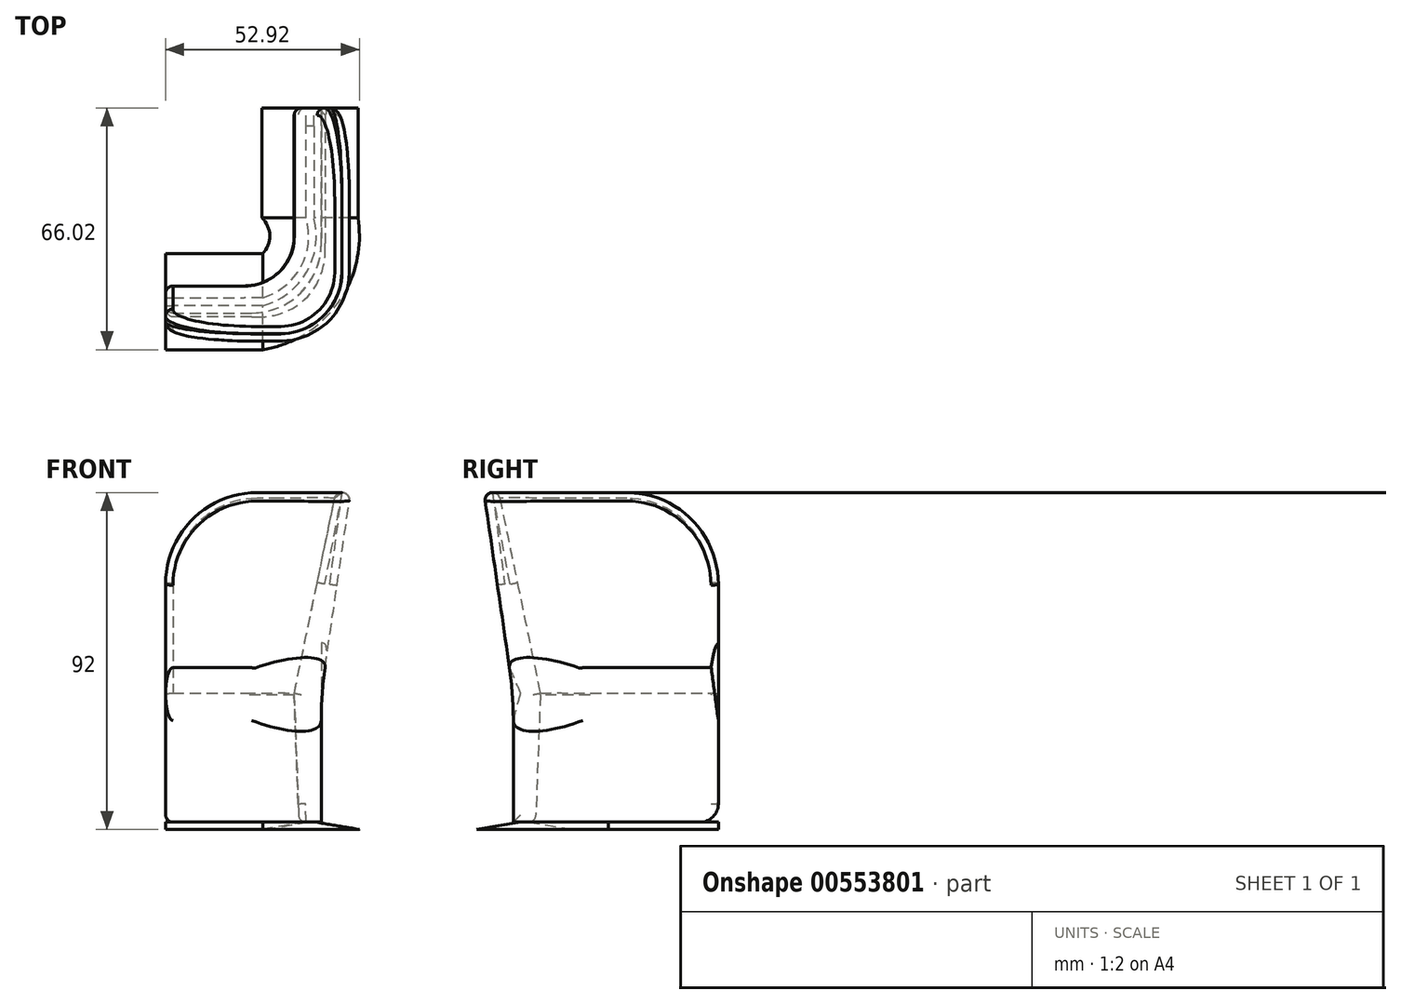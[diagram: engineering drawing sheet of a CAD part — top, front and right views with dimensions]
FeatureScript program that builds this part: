
annotation { "Feature Type Name" : "Feature", "Feature Type Description" : "" }
export const myFeature = defineFeature(function(context is Context, id is Id, definition is map)
    precondition{}
    {
        {
            var Q0;
            Q0=qCreatedBy(makeId("Top.planeOp"),FACE);
            var sketch = newSketch(context, id + "F0", { "sketchPlane" : qUnion([Q0])});
            skLineSegment(sketch, "E0", {"start": v(0, -50) * mm, "end": v(0, -15) * mm});
            skLineSegment(sketch, "E1", {"start": v(-15, 0) * mm, "end": v(-40, 0) * mm});
            skLineSegment(sketch, "E2", {"start": v(-40, 0) * mm, "end": v(-40, 6) * mm});
            skLineSegment(sketch, "E3", {"start": v(-40, 6) * mm, "end": v(-13, 6) * mm});
            skLineSegment(sketch, "E4", {"start": v(6, -13) * mm, "end": v(6, -50) * mm});
            skLineSegment(sketch, "E5", {"start": v(6, -50) * mm, "end": v(0, -50) * mm});
            skPoint(sketch, "E6.visualSharp", {"position": v(0, 0) * mm});
            skArc(sketch, "E6.filletArc", {"start": v(0, -15) * mm, "mid": v(-4.4, -4.4) * mm, "end": v(-15, 0) * mm});
            skArc(sketch, "E7.filletArc", {"start": v(6, -13) * mm, "mid": v(0.44, 0.44) * mm, "end": v(-13, 6) * mm});
            skSolve(sketch);
        }
        {
            var Q0;
            Q0=makeQuery(id+"F0.imprint","IMPRINT",FACE,{"disambiguationData":[TD([[makeQuery(id+"F0.imprint","IMPRINT",EDGE,{"derivedFrom":sQuery(id+"F0.wireOp",EDGE,"E0")}),-1.0]])]});
            extrude(context, id + "F1", {"entities" : qUnion([Q0]), "depth" : 40 * mm});
        }
        {
            var Q0;
            Q0=makeQuery(id+"F1.opExtrude","CAP_FACE",FACE,{"disambiguationData":[OSD([sQuery(id+"F0.wireOp",EDGE,"E0"),sQuery(id+"F0.wireOp",EDGE,"E1"),sQuery(id+"F0.wireOp",EDGE,"E2"),sQuery(id+"F0.wireOp",EDGE,"E3"),sQuery(id+"F0.wireOp",EDGE,"E4"),sQuery(id+"F0.wireOp",EDGE,"E5"),sQuery(id+"F0.wireOp",EDGE,"E6.filletArc"),sQuery(id+"F0.wireOp",EDGE,"E7.filletArc")])],"isStart":false});
            var sketch = newSketch(context, id + "F2", { "sketchPlane" : qUnion([Q0])});
            skLineSegment(sketch, "E8.0", {"start": v(-15, -1.5) * mm, "end": v(-40, -1.5) * mm});
            skArc(sketch, "E8.1", {"start": v(-1.5, -15) * mm, "mid": v(-5.45, -5.45) * mm, "end": v(-15, -1.5) * mm});
            skLineSegment(sketch, "E8.2", {"start": v(-1.5, -50) * mm, "end": v(-1.5, -15) * mm});
            skLineSegment(sketch, "E9", {"start": v(-40, -1.5) * mm, "end": v(-40, 6) * mm});
            skLineSegment(sketch, "E10", {"start": v(-1.5, -50) * mm, "end": v(6, -50) * mm});
            skLineSegment(sketch, "E11.0", {"start": v(-40, 6) * mm, "end": v(-13, 6) * mm});
            skArc(sketch, "E11.1", {"start": v(6, -13) * mm, "mid": v(0.44, 0.44) * mm, "end": v(-13, 6) * mm});
            skLineSegment(sketch, "E11.2", {"start": v(6, -13) * mm, "end": v(6, -50) * mm});
            skSolve(sketch);
        }
        {
            var Q0;
            Q0=makeQuery(id+"F1.opExtrude","SWEPT_FACE",FACE,{"disambiguationData":[OSD([sQuery(id+"F0.wireOp",EDGE,"E2")])]});
            var sketch = newSketch(context, id + "F3", { "sketchPlane" : qUnion([Q0])});
            skLineSegment(sketch, "E12", {"start": v(1.5, 40) * mm, "end": v(0, 0) * mm});
            skLineSegment(sketch, "E13", {"start": v(1.5, 40) * mm, "end": v(0, 40) * mm});
            skLineSegment(sketch, "E14", {"start": v(0, 40) * mm, "end": v(0, 0) * mm});
            skSolve(sketch);
        }
        {
            var Q0;
            Q0=makeQuery(id+"F1.opExtrude","SWEPT_FACE",FACE,{"disambiguationData":[OSD([sQuery(id+"F0.wireOp",EDGE,"E5")])]});
            var sketch = newSketch(context, id + "F4", { "sketchPlane" : qUnion([Q0])});
            skLineSegment(sketch, "E15", {"start": v(0, 0) * mm, "end": v(-1.5, 40) * mm});
            skLineSegment(sketch, "E16", {"start": v(-1.5, 40) * mm, "end": v(0, 40) * mm});
            skLineSegment(sketch, "E17", {"start": v(0, 40) * mm, "end": v(0, 0) * mm});
            skSolve(sketch);
        }
        {
            var Q0;
            Q0=makeQuery(id+"F3.imprint","IMPRINT",FACE,{"disambiguationData":[TD([[makeQuery(id+"F3.imprint","IMPRINT",EDGE,{"derivedFrom":sQuery(id+"F3.wireOp",EDGE,"E12")}),-1.0]])]});
            extrude(context, id + "F5", {"entities" : qUnion([Q0]), "oppositeDirection" : true, "depth" : 25 * mm});
        }
        {
            var Q0;
            Q0=sQuery(id+"F0.wireOp",VERTEX,"E6.filletArc.center");
            var Q1;
            Q1=makeQuery(id+"F5.opExtrude","CAP_EDGE",EDGE,{"disambiguationData":[OSD([sQuery(id+"F3.wireOp",EDGE,"E12")])],"isStart":false});
            cPlane(context, id + "F6", {"entities" : qUnion([Q0, Q1]), "cplaneType" : CPlaneType.LINE_ANGLE, "offset" : 25 * mm, "angle" : 0 * degree, "width" : 150 * mm, "height" : 150 * mm});
        }
        {
            var Q0;
            Q0=qCreatedBy(id+"F6.planeOp",FACE);
            var sketch = newSketch(context, id + "F7", { "sketchPlane" : qUnion([Q0])});
            skLineSegment(sketch, "E18", {"start": v(15, 0) * mm, "end": v(15, 39.86) * mm, "construction": true});
            skSolve(sketch);
        }
        {
            var Q0;
            Q0=makeQuery(id+"F5.opExtrude","CAP_FACE",FACE,{"disambiguationData":[OSD([sQuery(id+"F3.wireOp",EDGE,"E12"),sQuery(id+"F3.wireOp",EDGE,"E13"),sQuery(id+"F3.wireOp",EDGE,"E14")])],"isStart":false});
            var sketch = newSketch(context, id + "F8", { "sketchPlane" : qUnion([Q0])});
            skLineSegment(sketch, "E19.0", {"start": v(-1.5, 40) * mm, "end": v(0, 0) * mm});
            skLineSegment(sketch, "E19.1", {"start": v(-1.5, 40) * mm, "end": v(0, 40) * mm});
            skLineSegment(sketch, "E19.2", {"start": v(0, 40) * mm, "end": v(0, 0) * mm});
            skSolve(sketch);
        }
        {
            var Q0;
            Q0=makeQuery(id+"F8.imprint","IMPRINT",FACE,{"disambiguationData":[TD([[makeQuery(id+"F8.imprint","IMPRINT",EDGE,{"derivedFrom":sQuery(id+"F8.wireOp",EDGE,"E19.0")}),1.0]])]});
            var Q1;
            Q1=sQuery(id+"F7.wireOp",EDGE,"E18");
            revolve(context, id + "F9", {"entities" : qUnion([Q0]), "axis" : qUnion([Q1]), "revolveType" : RevolveType.ONE_DIRECTION, "oppositeDirection" : true, "angle" : 90 * degree});
        }
        {
            var Q0;
            Q0=makeQuery(id+"F4.imprint","IMPRINT",FACE,{"disambiguationData":[TD([[makeQuery(id+"F4.imprint","IMPRINT",EDGE,{"derivedFrom":sQuery(id+"F4.wireOp",EDGE,"E15")}),-1.0]])]});
            extrude(context, id + "F10", {"entities" : qUnion([Q0]), "endBound" : BoundingType.UP_TO_NEXT, "oppositeDirection" : true, "depth" : 25 * mm});
        }
        {
            var Q0;
            Q0=qCreatedBy(makeId("Front.planeOp"),FACE);
            var sketch = newSketch(context, id + "F11", { "sketchPlane" : qUnion([Q0])});
            skLineSegment(sketch, "E20.bottom", {"start": v(-36.5, 0) * mm, "end": v(-106.11, 0) * mm});
            skLineSegment(sketch, "E20.top", {"start": v(-36.5, 40) * mm, "end": v(-106.11, 40) * mm});
            skLineSegment(sketch, "E20.left", {"start": v(-36.5, 0) * mm, "end": v(-36.5, 40) * mm});
            skLineSegment(sketch, "E20.right", {"start": v(-106.11, 0) * mm, "end": v(-106.11, 40) * mm});
            skPoint(sketch, "E20.middle", {"position": v(-71.3, 20) * mm});
            skSolve(sketch);
        }
        {
            var Q0;
            Q0=qSketchRegion(id+"F11",true);
            extrude(context, id + "F12", {"entities" : qUnion([Q0]), "operationType" : NewBodyOperationType.REMOVE, "endBound" : BoundingType.SYMMETRIC, "oppositeDirection" : true, "depth" : 25 * mm});
        }
        {
            var Q0;
            Q0=qCreatedBy(makeId("Front.planeOp"),FACE);
            var sketch = newSketch(context, id + "F13", { "sketchPlane" : qUnion([Q0])});
            skLineSegment(sketch, "E21", {"start": v(6, 20) * mm, "end": v(-36.5, 20) * mm, "construction": true});
            skLineSegment(sketch, "E22.bottom", {"start": v(-36.5, 37.5) * mm, "end": v(6, 37.5) * mm});
            skLineSegment(sketch, "E22.top", {"start": v(-36.5, 46.2) * mm, "end": v(6, 46.2) * mm});
            skLineSegment(sketch, "E22.left", {"start": v(-36.5, 37.5) * mm, "end": v(-36.5, 46.2) * mm});
            skLineSegment(sketch, "E22.right", {"start": v(6, 37.5) * mm, "end": v(6, 46.2) * mm});
            skPoint(sketch, "E22.middle", {"position": v(-15.25, 41.85) * mm});
            skLineSegment(sketch, "E23.MirrorCS", {"start": v(-36.5, -6.2) * mm, "end": v(6, -6.2) * mm});
            skLineSegment(sketch, "E24.MirrorCS", {"start": v(-36.5, 2.5) * mm, "end": v(6, 2.5) * mm});
            skPoint(sketch, "E25.MirrorP", {"position": v(-15.25, -1.85) * mm});
            skLineSegment(sketch, "E26.MirrorCS", {"start": v(-36.5, 2.5) * mm, "end": v(-36.5, -6.2) * mm});
            skLineSegment(sketch, "E27.MirrorCS", {"start": v(6, 2.5) * mm, "end": v(6, -6.2) * mm});
            skSolve(sketch);
        }
        {
            var Q0;
            Q0=makeQuery(id+"F13.imprint","IMPRINT",FACE,{"disambiguationData":[TD([[makeQuery(id+"F13.imprint","IMPRINT",EDGE,{"derivedFrom":sQuery(id+"F13.wireOp",EDGE,"E22.bottom")}),1.0]])]});
            var Q1;
            Q1=makeQuery(id+"F13.imprint","IMPRINT",FACE,{"disambiguationData":[TD([[makeQuery(id+"F13.imprint","IMPRINT",EDGE,{"derivedFrom":sQuery(id+"F13.wireOp",EDGE,"E23.MirrorCS")}),1.0]])]});
            extrude(context, id + "F14", {"entities" : qUnion([Q0, Q1]), "operationType" : NewBodyOperationType.REMOVE, "endBound" : BoundingType.SYMMETRIC, "depth" : 200 * mm});
        }
        {
            var Q0;
            {var subQ5=sQuery(id+"F0.wireOp",EDGE,"E0");Q0=makeQuery(id+"F14.boolean.opBoolean","COPY",FACE,{"disambiguationData":[TD([makeQuery(id+"F1.opExtrude","SWEPT_FACE",FACE,{"disambiguationData":[OSD([subQ5])]})])],"derivedFrom":makeQuery(id+"F14.opExtrude","SWEPT_FACE",FACE,{"disambiguationData":[OSD([sQuery(id+"F13.wireOp",EDGE,"E22.bottom")])]})});}
            var sketch = newSketch(context, id + "F15", { "sketchPlane" : qUnion([Q0])});
            skLineSegment(sketch, "E28.1", {"start": v(-1.4, -15) * mm, "end": v(-1.4, -50) * mm});
            skLineSegment(sketch, "E28.2", {"start": v(-36.5, -1.4) * mm, "end": v(-15, -1.4) * mm});
            skArc(sketch, "E28.4.2", {"start": v(-15, -1.4) * mm, "mid": v(-5.39, -5.39) * mm, "end": v(-1.4, -15) * mm});
            skPoint(sketch, "E29.0", {"position": v(-36.5, 3) * mm});
            skLineSegment(sketch, "E30.0", {"start": v(-36.5, 0) * mm, "end": v(-36.5, 6) * mm});
            skLineSegment(sketch, "E30.1", {"start": v(-36.5, -1.4) * mm, "end": v(-36.5, 0) * mm});
            skPoint(sketch, "E30.2", {"position": v(-36.5, -0.7) * mm});
            skLineSegment(sketch, "E31.0", {"start": v(-36.5, 6) * mm, "end": v(-13, 6) * mm});
            skArc(sketch, "E32.0", {"start": v(6, -13) * mm, "mid": v(0.44, 0.44) * mm, "end": v(-13, 6) * mm});
            skLineSegment(sketch, "E33.0", {"start": v(6, -50) * mm, "end": v(6, -13) * mm});
            skLineSegment(sketch, "E34.0", {"start": v(6, -50) * mm, "end": v(0, -50) * mm});
            skLineSegment(sketch, "E35.0", {"start": v(0, -50) * mm, "end": v(-1.4, -50) * mm});
            skSolve(sketch);
        }
        {
            var Q0;
            Q0=makeQuery(id+"F15.imprint","IMPRINT",FACE,{"disambiguationData":[TD([[makeQuery(id+"F15.imprint","IMPRINT",EDGE,{"derivedFrom":sQuery(id+"F15.wireOp",EDGE,"E30.0")}),-1.0]])]});
            cPlane(context, id + "F16", {"entities" : qUnion([Q0]), "cplaneType" : CPlaneType.OFFSET, "offset" : 55 * mm, "width" : 150 * mm, "height" : 150 * mm});
        }
        {
            var Q0;
            Q0=qCreatedBy(id+"F16.planeOp",FACE);
            var sketch = newSketch(context, id + "F17", { "sketchPlane" : qUnion([Q0])});
            skLineSegment(sketch, "E36", {"start": v(-36.5, 10) * mm, "end": v(-36.5, 14) * mm});
            skLineSegment(sketch, "E37", {"start": v(-36.5, 14) * mm, "end": v(-5, 14) * mm});
            skLineSegment(sketch, "E38", {"start": v(14, -5) * mm, "end": v(14, -50) * mm});
            skLineSegment(sketch, "E39", {"start": v(14, -50) * mm, "end": v(10, -50) * mm});
            skLineSegment(sketch, "E40", {"start": v(10, -50) * mm, "end": v(10, -5) * mm});
            skLineSegment(sketch, "E41", {"start": v(-5, 10) * mm, "end": v(-36.5, 10) * mm});
            skPoint(sketch, "E42.visualSharp", {"position": v(10, 10) * mm});
            skArc(sketch, "E42.filletArc", {"start": v(10, -5) * mm, "mid": v(5.6, 5.6) * mm, "end": v(-5, 10) * mm});
            skPoint(sketch, "E43.visualSharp", {"position": v(14, 14) * mm});
            skArc(sketch, "E43.filletArc", {"start": v(14, -5) * mm, "mid": v(8.44, 8.44) * mm, "end": v(-5, 14) * mm});
            skSolve(sketch);
        }
        {
            var Q0;
            {var subQ6=sQuery(id+"F0.wireOp",EDGE,"E1");Q0=makeQuery(id+"F12.boolean.opBoolean","COPY",FACE,{"disambiguationData":[TD([makeQuery(id+"F1.opExtrude","SWEPT_FACE",FACE,{"disambiguationData":[OSD([subQ6])]})])],"derivedFrom":makeQuery(id+"F12.opExtrude","SWEPT_FACE",FACE,{"disambiguationData":[OSD([sQuery(id+"F11.wireOp",EDGE,"E20.left")])]})});}
            var sketch = newSketch(context, id + "F18", { "sketchPlane" : qUnion([Q0])});
            skLineSegment(sketch, "E44", {"start": v(-6, 37.5) * mm, "end": v(-14, 92.5) * mm});
            skLineSegment(sketch, "E45", {"start": v(-10, 92.5) * mm, "end": v(1.4, 37.5) * mm});
            skSolve(sketch);
        }
        {
            var Q0;
            Q0=makeQuery(id+"F1.opExtrude","SWEPT_FACE",FACE,{"disambiguationData":[OSD([sQuery(id+"F0.wireOp",EDGE,"E5")])]});
            var sketch = newSketch(context, id + "F19", { "sketchPlane" : qUnion([Q0])});
            skLineSegment(sketch, "E46", {"start": v(-1.4, 37.5) * mm, "end": v(10, 92.5) * mm});
            skLineSegment(sketch, "E47", {"start": v(14, 92.5) * mm, "end": v(6, 37.5) * mm});
            skSolve(sketch);
        }
        {
            var Q0;
            Q0=qSketchRegion(id+"F15",true);
            var Q1;
            Q1=qSketchRegion(id+"F17",true);
            var Q2;
            Q2=sQuery(id+"F18.wireOp",EDGE,"E44");
            var Q3;
            Q3=sQuery(id+"F19.wireOp",EDGE,"E46");
            var Q4;
            Q4=sQuery(id+"F18.wireOp",EDGE,"E45");
            var Q5;
            Q5=sQuery(id+"F19.wireOp",EDGE,"E47");
            loft(context, id + "F20", {"addGuides" : true, "sheetProfilesArray" : [{ "sheetProfileEntities" : qUnion([Q0]) }, { "sheetProfileEntities" : qUnion([Q1]) }], "guidesArray" : [{ "guideEntities" : qUnion([Q2]), "guideDerivativeType" : LoftGuideDerivativeType.DEFAULT, "guideDerivativeMagnitude" : 1 }, { "guideEntities" : qUnion([Q3]), "guideDerivativeType" : LoftGuideDerivativeType.DEFAULT, "guideDerivativeMagnitude" : 1 }, { "guideEntities" : qUnion([Q4]), "guideDerivativeType" : LoftGuideDerivativeType.DEFAULT, "guideDerivativeMagnitude" : 1 }, { "guideEntities" : qUnion([Q5]), "guideDerivativeType" : LoftGuideDerivativeType.DEFAULT, "guideDerivativeMagnitude" : 1 }]});
        }
        {
            var Q0;
            Q0=makeQuery(id+"F20.opLoft","MID_CAP_EDGE",EDGE,{"disambiguationData":[OSD([sQuery(id+"F15.wireOp",EDGE,"E30.0"),sQuery(id+"F15.wireOp",EDGE,"E31.0"),sQuery(id+"F17.wireOp",EDGE,"E36"),sQuery(id+"F17.wireOp",EDGE,"E41")])],"capPos":1.0});
            var Q1;
            Q1=makeQuery(id+"F20.opLoft","MID_CAP_EDGE",EDGE,{"disambiguationData":[OSD([sQuery(id+"F15.wireOp",EDGE,"E28.1"),sQuery(id+"F15.wireOp",EDGE,"E35.0"),sQuery(id+"F17.wireOp",EDGE,"E39"),sQuery(id+"F17.wireOp",EDGE,"E40")])],"capPos":1.0});
            fillet(context, id + "F21", {"entities" : qUnion([Q0, Q1]), "radius" : 25 * mm, "tangentPropagation" : true, "allowEdgeOverflow" : false});
        }
        {
            var Q0;
            {var subQ6=sQuery(id+"F0.wireOp",EDGE,"E1");var subQ8=sQuery(id+"F13.wireOp",EDGE,"E24.MirrorCS");Q0=makeQuery(id+"F14.boolean.opBoolean","COPY",EDGE,{"disambiguationData":[topologyDisambiguationEdgeConnected([makeQuery(id+"F12.boolean.opBoolean","COPY",FACE,{"disambiguationData":[TD([makeQuery(id+"F1.opExtrude","SWEPT_FACE",FACE,{"disambiguationData":[OSD([subQ6])]})])],"derivedFrom":makeQuery(id+"F12.opExtrude","SWEPT_FACE",FACE,{"disambiguationData":[OSD([sQuery(id+"F11.wireOp",EDGE,"E20.left")])]})})])],"derivedFrom":makeQuery(id+"F14.opExtrude","SWEPT_EDGE",EDGE,{"disambiguationData":[OSD([subQ8,sQuery(id+"F13.wireOp",EDGE,"E26.MirrorCS")])]})});}
            var Q1;
            Q1=makeQuery(id+"F14.boolean.opBoolean","INTERSECT",EDGE,{"derivedFrom":[makeQuery(id+"F1.opExtrude","SWEPT_FACE",FACE,{"disambiguationData":[OSD([sQuery(id+"F0.wireOp",EDGE,"E5")])]}),makeQuery(id+"F14.opExtrude","SWEPT_FACE",FACE,{"disambiguationData":[OSD([sQuery(id+"F13.wireOp",EDGE,"E24.MirrorCS")])]})]});
            var Q2;
            {var subQ0=sQuery(id+"F13.wireOp",EDGE,"E24.MirrorCS");Q2=makeQuery(id+"F14.boolean.opBoolean","COPY",EDGE,{"disambiguationData":[topologyDisambiguationEdgeConnected([makeQuery(id+"F12.boolean.opBoolean","COPY",FACE,{"disambiguationData":[TD([makeQuery(id+"F5.opExtrude","SWEPT_FACE",FACE,{"disambiguationData":[OSD([sQuery(id+"F3.wireOp",EDGE,"E12")])]})])],"derivedFrom":makeQuery(id+"F12.opExtrude","SWEPT_FACE",FACE,{"disambiguationData":[OSD([sQuery(id+"F11.wireOp",EDGE,"E20.left")])]})})])],"derivedFrom":makeQuery(id+"F14.opExtrude","SWEPT_EDGE",EDGE,{"disambiguationData":[OSD([subQ0,sQuery(id+"F13.wireOp",EDGE,"E26.MirrorCS")])]})});}
            var Q3;
            Q3=makeQuery(id+"F14.boolean.opBoolean","INTERSECT",EDGE,{"derivedFrom":[makeQuery(id+"F10.opExtrude","CAP_FACE",FACE,{"disambiguationData":[OSD([sQuery(id+"F4.wireOp",EDGE,"E15"),sQuery(id+"F4.wireOp",EDGE,"E16"),sQuery(id+"F4.wireOp",EDGE,"E17")])],"isStart":true}),makeQuery(id+"F14.opExtrude","SWEPT_FACE",FACE,{"disambiguationData":[OSD([sQuery(id+"F13.wireOp",EDGE,"E24.MirrorCS")])]})]});
            fillet(context, id + "F22", {"entities" : qUnion([Q0, Q1, Q2, Q3]), "radius" : 5 * mm, "tangentPropagation" : true, "allowEdgeOverflow" : false});
        }
        {
            var Q0;
            Q0=makeQuery(id+"F1.opExtrude","SWEPT_BODY",BODY,{"disambiguationData":[OSD([sQuery(id+"F0.wireOp",EDGE,"E0"),sQuery(id+"F0.wireOp",EDGE,"E1"),sQuery(id+"F0.wireOp",EDGE,"E2"),sQuery(id+"F0.wireOp",EDGE,"E3"),sQuery(id+"F0.wireOp",EDGE,"E4"),sQuery(id+"F0.wireOp",EDGE,"E5"),sQuery(id+"F0.wireOp",EDGE,"E6.filletArc"),sQuery(id+"F0.wireOp",EDGE,"E7.filletArc")])]});
            var Q1;
            Q1=makeQuery(id+"F5.opExtrude","SWEPT_BODY",BODY,{"disambiguationData":[OSD([sQuery(id+"F3.wireOp",EDGE,"E12"),sQuery(id+"F3.wireOp",EDGE,"E13"),sQuery(id+"F3.wireOp",EDGE,"E14")])]});
            var Q2;
            Q2=makeQuery(id+"F9.opRevolve","SWEPT_BODY",BODY,{"disambiguationData":[OSD([sQuery(id+"F8.wireOp",EDGE,"E19.0"),sQuery(id+"F8.wireOp",EDGE,"E19.1"),sQuery(id+"F8.wireOp",EDGE,"E19.2")])]});
            var Q3;
            Q3=makeQuery(id+"F10.opExtrude","SWEPT_BODY",BODY,{"disambiguationData":[OSD([sQuery(id+"F4.wireOp",EDGE,"E15"),sQuery(id+"F4.wireOp",EDGE,"E16"),sQuery(id+"F4.wireOp",EDGE,"E17")])]});
            var Q4;
            Q4=makeQuery(id+"F20.opLoft","SWEPT_BODY",BODY,{"disambiguationData":[OSD([makeQuery(id+"F15.imprint","IMPRINT",FACE,{"disambiguationData":[TD([[makeQuery(id+"F15.imprint","IMPRINT",EDGE,{"derivedFrom":sQuery(id+"F15.wireOp",EDGE,"E28.1")}),1.0]])]}),makeQuery(id+"F17.imprint","IMPRINT",FACE,{"disambiguationData":[TD([[makeQuery(id+"F17.imprint","IMPRINT",EDGE,{"derivedFrom":sQuery(id+"F17.wireOp",EDGE,"E36")}),-1.0]])]}),sQuery(id+"F18.wireOp",EDGE,"E44"),sQuery(id+"F18.wireOp",EDGE,"E45"),sQuery(id+"F19.wireOp",EDGE,"E46"),sQuery(id+"F19.wireOp",EDGE,"E47")])]});
            booleanBodies(context, id + "F23", {"operationType" : BooleanOperationType.UNION, "tools" : qUnion([Q0, Q1, Q2, Q3, Q4])});
        }
        {
            var Q0;
            Q0=makeQuery(id+"F20.opLoft","CAP_FACE",FACE,{"disambiguationData":[OSD([makeQuery(id+"F17.imprint","IMPRINT",FACE,{"disambiguationData":[TD([[makeQuery(id+"F17.imprint","IMPRINT",EDGE,{"derivedFrom":sQuery(id+"F17.wireOp",EDGE,"E36")}),-1.0]])]})])],"isStart":true});
            fillet(context, id + "F24", {"entities" : qUnion([Q0]), "radius" : 2 * mm, "tangentPropagation" : true, "allowEdgeOverflow" : false});
        }
        {
            var Q0;
            {var subQ6=sQuery(id+"F0.wireOp",EDGE,"E1");var subQ8=makeQuery(id+"F12.opExtrude","SWEPT_FACE",FACE,{"disambiguationData":[OSD([sQuery(id+"F11.wireOp",EDGE,"E20.left")])]});Q0=makeQuery(id+"F23.opBoolean","MERGE",FACE,{"derivedFrom":[makeQuery(id+"F20.opLoft","SWEPT_FACE",FACE,{"disambiguationData":[OSD([subQ6,sQuery(id+"F13.wireOp",EDGE,"E22.bottom"),sQuery(id+"F15.wireOp",EDGE,"E28.2"),sQuery(id+"F15.wireOp",EDGE,"E30.0"),sQuery(id+"F15.wireOp",EDGE,"E30.1"),sQuery(id+"F15.wireOp",EDGE,"E31.0"),sQuery(id+"F17.wireOp",EDGE,"E36"),sQuery(id+"F17.wireOp",EDGE,"E41"),sQuery(id+"F18.wireOp",VERTEX,"E45.start"),sQuery(id+"F18.wireOp",VERTEX,"E45.end"),sQuery(id+"F18.wireOp",EDGE,"E45")])]}),makeQuery(id+"F12.boolean.opBoolean","COPY",FACE,{"disambiguationData":[TD([makeQuery(id+"F5.opExtrude","SWEPT_FACE",FACE,{"disambiguationData":[OSD([sQuery(id+"F3.wireOp",EDGE,"E12")])]})])],"derivedFrom":subQ8}),makeQuery(id+"F12.boolean.opBoolean","COPY",FACE,{"disambiguationData":[TD([makeQuery(id+"F1.opExtrude","SWEPT_FACE",FACE,{"disambiguationData":[OSD([subQ6])]})])],"derivedFrom":subQ8})]});}
            fillet(context, id + "F25", {"entities" : qUnion([Q0]), "radius" : 2 * mm, "tangentPropagation" : true, "allowEdgeOverflow" : false});
        }
        {
            var Q0;
            Q0=makeQuery(id+"F23.opBoolean","MERGE",EDGE,{"derivedFrom":[makeQuery(id+"F14.boolean.opBoolean","INTERSECT",EDGE,{"derivedFrom":[makeQuery(id+"F1.opExtrude","SWEPT_FACE",FACE,{"disambiguationData":[OSD([sQuery(id+"F0.wireOp",EDGE,"E3")])]}),makeQuery(id+"F14.opExtrude","SWEPT_FACE",FACE,{"disambiguationData":[OSD([sQuery(id+"F13.wireOp",EDGE,"E22.bottom")])]})]}),makeQuery(id+"F20.opLoft","MID_CAP_EDGE",EDGE,{"disambiguationData":[OSD([sQuery(id+"F15.wireOp",EDGE,"E30.0"),sQuery(id+"F15.wireOp",EDGE,"E31.0"),sQuery(id+"F15.wireOp",EDGE,"E32.0")])],"capPos":0.0})]});
            fillet(context, id + "F26", {"entities" : qUnion([Q0]), "radius" : 100 * mm, "tangentPropagation" : true, "allowEdgeOverflow" : false});
        }
        {
            var Q0;
            Q0=makeQuery(id+"F23.opBoolean","MERGE",FACE,{"derivedFrom":[makeQuery(id+"F20.opLoft","SWEPT_FACE",FACE,{"disambiguationData":[OSD([sQuery(id+"F0.wireOp",EDGE,"E0"),sQuery(id+"F13.wireOp",EDGE,"E22.bottom"),sQuery(id+"F15.wireOp",EDGE,"E28.1"),sQuery(id+"F15.wireOp",EDGE,"E34.0"),sQuery(id+"F15.wireOp",EDGE,"E35.0"),sQuery(id+"F17.wireOp",EDGE,"E39"),sQuery(id+"F17.wireOp",EDGE,"E40"),sQuery(id+"F19.wireOp",VERTEX,"E46.start"),sQuery(id+"F19.wireOp",VERTEX,"E46.end"),sQuery(id+"F19.wireOp",EDGE,"E46")])]}),makeQuery(id+"F1.opExtrude","SWEPT_FACE",FACE,{"disambiguationData":[OSD([sQuery(id+"F0.wireOp",EDGE,"E5")])]}),makeQuery(id+"F10.opExtrude","CAP_FACE",FACE,{"disambiguationData":[OSD([sQuery(id+"F4.wireOp",EDGE,"E15"),sQuery(id+"F4.wireOp",EDGE,"E16"),sQuery(id+"F4.wireOp",EDGE,"E17")])],"isStart":true})]});
            var sketch = newSketch(context, id + "F27", { "sketchPlane" : qUnion([Q0])});
            skLineSegment(sketch, "E48", {"start": v(1.83, 2.5) * mm, "end": v(-10.2, 0.5) * mm});
            skLineSegment(sketch, "E49", {"start": v(16.02, 0.5) * mm, "end": v(4, 2.5) * mm});
            skLineSegment(sketch, "E50", {"start": v(4, 2.5) * mm, "end": v(1.83, 2.5) * mm});
            skLineSegment(sketch, "E51", {"start": v(2.92, 2.5) * mm, "end": v(2.92, 0) * mm, "construction": true});
            skLineSegment(sketch, "E52", {"start": v(-10.2, 0.5) * mm, "end": v(16.02, 0.5) * mm});
            skSolve(sketch);
        }
        {
            var Q0;
            Q0=makeQuery(id+"F27.imprint","IMPRINT",FACE,{"disambiguationData":[TD([[makeQuery(id+"F27.imprint","IMPRINT",EDGE,{"derivedFrom":sQuery(id+"F27.wireOp",EDGE,"E48")}),1.0]])]});
            var Q1;
            {var subQ5=sQuery(id+"F0.wireOp",EDGE,"E0");var subQ11=makeQuery(id+"F14.opExtrude","SWEPT_FACE",FACE,{"disambiguationData":[OSD([sQuery(id+"F13.wireOp",EDGE,"E24.MirrorCS")])]});var subQ12=sQuery(id+"F4.wireOp",EDGE,"E15");var subQ13=makeQuery(id+"F10.opExtrude","SWEPT_FACE",FACE,{"disambiguationData":[OSD([subQ12])]});var subQ16=sQuery(id+"F3.wireOp",EDGE,"E12");var subQ17=makeQuery(id+"F5.opExtrude","SWEPT_FACE",FACE,{"disambiguationData":[OSD([subQ16])]});var subQ21=sQuery(id+"F8.wireOp",EDGE,"E19.0");Q1=makeQuery(id+"F25.opFillet","BLEND_EDGE",EDGE,{"blendedFrom":[makeQuery(id+"F14.boolean.opBoolean","INTERSECT",EDGE,{"derivedFrom":[subQ13,subQ11]}),makeQuery(id+"F23.opBoolean","MERGE",FACE,{"derivedFrom":[makeQuery(id+"F14.boolean.opBoolean","COPY",FACE,{"disambiguationData":[TD([makeQuery(id+"F9.opRevolve","SWEPT_FACE",FACE,{"disambiguationData":[OSD([subQ21])]})])],"derivedFrom":subQ11}),makeQuery(id+"F14.boolean.opBoolean","COPY",FACE,{"disambiguationData":[TD([subQ17])],"derivedFrom":subQ11}),makeQuery(id+"F14.boolean.opBoolean","COPY",FACE,{"disambiguationData":[TD([subQ13])],"derivedFrom":subQ11}),makeQuery(id+"F14.boolean.opBoolean","COPY",FACE,{"disambiguationData":[TD([makeQuery(id+"F1.opExtrude","SWEPT_FACE",FACE,{"disambiguationData":[OSD([subQ5])]})])],"derivedFrom":subQ11})]})],"blendedInto":[makeQuery(id+"F23.opBoolean","MERGE",FACE,{"derivedFrom":[makeQuery(id+"F14.boolean.opBoolean","COPY",FACE,{"disambiguationData":[TD([makeQuery(id+"F9.opRevolve","SWEPT_FACE",FACE,{"disambiguationData":[OSD([subQ21])]})])],"derivedFrom":subQ11}),makeQuery(id+"F14.boolean.opBoolean","COPY",FACE,{"disambiguationData":[TD([subQ17])],"derivedFrom":subQ11}),makeQuery(id+"F14.boolean.opBoolean","COPY",FACE,{"disambiguationData":[TD([subQ13])],"derivedFrom":subQ11}),makeQuery(id+"F14.boolean.opBoolean","COPY",FACE,{"disambiguationData":[TD([makeQuery(id+"F1.opExtrude","SWEPT_FACE",FACE,{"disambiguationData":[OSD([subQ5])]})])],"derivedFrom":subQ11})]})]});}
            var Q2;
            {var subQ5=sQuery(id+"F0.wireOp",EDGE,"E0");var subQ11=makeQuery(id+"F14.opExtrude","SWEPT_FACE",FACE,{"disambiguationData":[OSD([sQuery(id+"F13.wireOp",EDGE,"E24.MirrorCS")])]});var subQ12=sQuery(id+"F4.wireOp",EDGE,"E15");var subQ15=sQuery(id+"F3.wireOp",EDGE,"E12");var subQ16=makeQuery(id+"F5.opExtrude","SWEPT_FACE",FACE,{"disambiguationData":[OSD([subQ15])]});var subQ20=sQuery(id+"F8.wireOp",EDGE,"E19.0");var subQ21=makeQuery(id+"F9.opRevolve","SWEPT_FACE",FACE,{"disambiguationData":[OSD([subQ20])]});Q2=makeQuery(id+"F25.opFillet","BLEND_EDGE",EDGE,{"blendedFrom":[makeQuery(id+"F14.boolean.opBoolean","INTERSECT",EDGE,{"derivedFrom":[subQ21,subQ11]}),makeQuery(id+"F23.opBoolean","MERGE",FACE,{"derivedFrom":[makeQuery(id+"F14.boolean.opBoolean","COPY",FACE,{"disambiguationData":[TD([subQ21])],"derivedFrom":subQ11}),makeQuery(id+"F14.boolean.opBoolean","COPY",FACE,{"disambiguationData":[TD([subQ16])],"derivedFrom":subQ11}),makeQuery(id+"F14.boolean.opBoolean","COPY",FACE,{"disambiguationData":[TD([makeQuery(id+"F10.opExtrude","SWEPT_FACE",FACE,{"disambiguationData":[OSD([subQ12])]})])],"derivedFrom":subQ11}),makeQuery(id+"F14.boolean.opBoolean","COPY",FACE,{"disambiguationData":[TD([makeQuery(id+"F1.opExtrude","SWEPT_FACE",FACE,{"disambiguationData":[OSD([subQ5])]})])],"derivedFrom":subQ11})]})],"blendedInto":[makeQuery(id+"F23.opBoolean","MERGE",FACE,{"derivedFrom":[makeQuery(id+"F14.boolean.opBoolean","COPY",FACE,{"disambiguationData":[TD([subQ21])],"derivedFrom":subQ11}),makeQuery(id+"F14.boolean.opBoolean","COPY",FACE,{"disambiguationData":[TD([subQ16])],"derivedFrom":subQ11}),makeQuery(id+"F14.boolean.opBoolean","COPY",FACE,{"disambiguationData":[TD([makeQuery(id+"F10.opExtrude","SWEPT_FACE",FACE,{"disambiguationData":[OSD([subQ12])]})])],"derivedFrom":subQ11}),makeQuery(id+"F14.boolean.opBoolean","COPY",FACE,{"disambiguationData":[TD([makeQuery(id+"F1.opExtrude","SWEPT_FACE",FACE,{"disambiguationData":[OSD([subQ5])]})])],"derivedFrom":subQ11})]})]});}
            var Q3;
            {var subQ5=sQuery(id+"F0.wireOp",EDGE,"E0");var subQ11=makeQuery(id+"F14.opExtrude","SWEPT_FACE",FACE,{"disambiguationData":[OSD([sQuery(id+"F13.wireOp",EDGE,"E24.MirrorCS")])]});var subQ12=sQuery(id+"F4.wireOp",EDGE,"E15");var subQ15=sQuery(id+"F3.wireOp",EDGE,"E12");var subQ16=makeQuery(id+"F5.opExtrude","SWEPT_FACE",FACE,{"disambiguationData":[OSD([subQ15])]});var subQ20=sQuery(id+"F8.wireOp",EDGE,"E19.0");Q3=makeQuery(id+"F25.opFillet","BLEND_EDGE",EDGE,{"blendedFrom":[makeQuery(id+"F14.boolean.opBoolean","INTERSECT",EDGE,{"derivedFrom":[subQ16,subQ11]}),makeQuery(id+"F23.opBoolean","MERGE",FACE,{"derivedFrom":[makeQuery(id+"F14.boolean.opBoolean","COPY",FACE,{"disambiguationData":[TD([makeQuery(id+"F9.opRevolve","SWEPT_FACE",FACE,{"disambiguationData":[OSD([subQ20])]})])],"derivedFrom":subQ11}),makeQuery(id+"F14.boolean.opBoolean","COPY",FACE,{"disambiguationData":[TD([subQ16])],"derivedFrom":subQ11}),makeQuery(id+"F14.boolean.opBoolean","COPY",FACE,{"disambiguationData":[TD([makeQuery(id+"F10.opExtrude","SWEPT_FACE",FACE,{"disambiguationData":[OSD([subQ12])]})])],"derivedFrom":subQ11}),makeQuery(id+"F14.boolean.opBoolean","COPY",FACE,{"disambiguationData":[TD([makeQuery(id+"F1.opExtrude","SWEPT_FACE",FACE,{"disambiguationData":[OSD([subQ5])]})])],"derivedFrom":subQ11})]})],"blendedInto":[makeQuery(id+"F23.opBoolean","MERGE",FACE,{"derivedFrom":[makeQuery(id+"F14.boolean.opBoolean","COPY",FACE,{"disambiguationData":[TD([makeQuery(id+"F9.opRevolve","SWEPT_FACE",FACE,{"disambiguationData":[OSD([subQ20])]})])],"derivedFrom":subQ11}),makeQuery(id+"F14.boolean.opBoolean","COPY",FACE,{"disambiguationData":[TD([subQ16])],"derivedFrom":subQ11}),makeQuery(id+"F14.boolean.opBoolean","COPY",FACE,{"disambiguationData":[TD([makeQuery(id+"F10.opExtrude","SWEPT_FACE",FACE,{"disambiguationData":[OSD([subQ12])]})])],"derivedFrom":subQ11}),makeQuery(id+"F14.boolean.opBoolean","COPY",FACE,{"disambiguationData":[TD([makeQuery(id+"F1.opExtrude","SWEPT_FACE",FACE,{"disambiguationData":[OSD([subQ5])]})])],"derivedFrom":subQ11})]})]});}
            sweep(context, id + "F28", {"operationType" : NewBodyOperationType.ADD, "profiles" : qUnion([Q0]), "path" : qUnion([Q1, Q2, Q3])});
        }
        {
            var Q0;
            Q0=makeQuery(id+"F28.opSweep","CAP_FACE",FACE,{"disambiguationData":[OSD([sQuery(id+"F3.wireOp",EDGE,"E12"),sQuery(id+"F13.wireOp",EDGE,"E24.MirrorCS"),sQuery(id+"F13.wireOp",EDGE,"E26.MirrorCS"),sQuery(id+"F27.wireOp",EDGE,"E48"),sQuery(id+"F27.wireOp",EDGE,"E49"),sQuery(id+"F27.wireOp",EDGE,"E50"),sQuery(id+"F27.wireOp",EDGE,"E52")])],"isStart":false});
            var Q1;
            {var subQ5=sQuery(id+"F0.wireOp",EDGE,"E0");var subQ11=makeQuery(id+"F14.opExtrude","SWEPT_FACE",FACE,{"disambiguationData":[OSD([sQuery(id+"F13.wireOp",EDGE,"E24.MirrorCS")])]});var subQ12=sQuery(id+"F4.wireOp",EDGE,"E15");var subQ15=sQuery(id+"F3.wireOp",EDGE,"E12");var subQ16=makeQuery(id+"F5.opExtrude","SWEPT_FACE",FACE,{"disambiguationData":[OSD([subQ15])]});var subQ20=sQuery(id+"F8.wireOp",EDGE,"E19.0");Q1=makeQuery(id+"F28.boolean.opBoolean","SPLIT",EDGE,{"derivedFrom":makeQuery(id+"F25.opFillet","BLEND_EDGE",EDGE,{"blendedFrom":[makeQuery(id+"F14.boolean.opBoolean","INTERSECT",EDGE,{"derivedFrom":[subQ16,subQ11]}),makeQuery(id+"F23.opBoolean","MERGE",FACE,{"derivedFrom":[makeQuery(id+"F14.boolean.opBoolean","COPY",FACE,{"disambiguationData":[TD([makeQuery(id+"F9.opRevolve","SWEPT_FACE",FACE,{"disambiguationData":[OSD([subQ20])]})])],"derivedFrom":subQ11}),makeQuery(id+"F14.boolean.opBoolean","COPY",FACE,{"disambiguationData":[TD([subQ16])],"derivedFrom":subQ11}),makeQuery(id+"F14.boolean.opBoolean","COPY",FACE,{"disambiguationData":[TD([makeQuery(id+"F10.opExtrude","SWEPT_FACE",FACE,{"disambiguationData":[OSD([subQ12])]})])],"derivedFrom":subQ11}),makeQuery(id+"F14.boolean.opBoolean","COPY",FACE,{"disambiguationData":[TD([makeQuery(id+"F1.opExtrude","SWEPT_FACE",FACE,{"disambiguationData":[OSD([subQ5])]})])],"derivedFrom":subQ11})]})],"blendedInto":[makeQuery(id+"F23.opBoolean","MERGE",FACE,{"derivedFrom":[makeQuery(id+"F14.boolean.opBoolean","COPY",FACE,{"disambiguationData":[TD([makeQuery(id+"F9.opRevolve","SWEPT_FACE",FACE,{"disambiguationData":[OSD([subQ20])]})])],"derivedFrom":subQ11}),makeQuery(id+"F14.boolean.opBoolean","COPY",FACE,{"disambiguationData":[TD([subQ16])],"derivedFrom":subQ11}),makeQuery(id+"F14.boolean.opBoolean","COPY",FACE,{"disambiguationData":[TD([makeQuery(id+"F10.opExtrude","SWEPT_FACE",FACE,{"disambiguationData":[OSD([subQ12])]})])],"derivedFrom":subQ11}),makeQuery(id+"F14.boolean.opBoolean","COPY",FACE,{"disambiguationData":[TD([makeQuery(id+"F1.opExtrude","SWEPT_FACE",FACE,{"disambiguationData":[OSD([subQ5])]})])],"derivedFrom":subQ11})]})]})});}
            sweep(context, id + "F29", {"operationType" : NewBodyOperationType.ADD, "profiles" : qUnion([Q0]), "path" : qUnion([Q1])});
        }
        {
            var Q0;
            Q0=makeQuery(id+"F29.opSweep","CAP_FACE",FACE,{"disambiguationData":[OSD([sQuery(id+"F3.wireOp",EDGE,"E12"),sQuery(id+"F13.wireOp",EDGE,"E24.MirrorCS"),sQuery(id+"F13.wireOp",EDGE,"E26.MirrorCS"),sQuery(id+"F27.wireOp",EDGE,"E48"),sQuery(id+"F27.wireOp",EDGE,"E49"),sQuery(id+"F27.wireOp",EDGE,"E50"),sQuery(id+"F27.wireOp",EDGE,"E52")])],"isStart":false});
            var sketch = newSketch(context, id + "F30", { "sketchPlane" : qUnion([Q0])});
            skLineSegment(sketch, "E53.0", {"start": v(10.2, 0.5) * mm, "end": v(-1.83, 2.5) * mm});
            skLineSegment(sketch, "E54.0", {"start": v(-16.02, 0.5) * mm, "end": v(10.2, 0.5) * mm});
            skLineSegment(sketch, "E55.0", {"start": v(-4, 2.5) * mm, "end": v(-16.02, 0.5) * mm});
            skLineSegment(sketch, "E56.0.2", {"start": v(-1.83, 2.5) * mm, "end": v(-4, 2.5) * mm});
            skSolve(sketch);
        }
        {
            var Q0;
            Q0=makeQuery(id+"F30.imprint","IMPRINT",FACE,{"disambiguationData":[TD([[makeQuery(id+"F30.imprint","IMPRINT",EDGE,{"derivedFrom":sQuery(id+"F30.wireOp",EDGE,"E54.0")}),1.0]])]});
            var Q1;
            {var subQ6=sQuery(id+"F0.wireOp",EDGE,"E1");var subQ8=makeQuery(id+"F12.opExtrude","SWEPT_FACE",FACE,{"disambiguationData":[OSD([sQuery(id+"F11.wireOp",EDGE,"E20.left")])]});Q1=makeQuery(id+"F23.opBoolean","MERGE",FACE,{"derivedFrom":[makeQuery(id+"F20.opLoft","SWEPT_FACE",FACE,{"disambiguationData":[OSD([subQ6,sQuery(id+"F13.wireOp",EDGE,"E22.bottom"),sQuery(id+"F15.wireOp",EDGE,"E28.2"),sQuery(id+"F15.wireOp",EDGE,"E30.0"),sQuery(id+"F15.wireOp",EDGE,"E30.1"),sQuery(id+"F15.wireOp",EDGE,"E31.0"),sQuery(id+"F17.wireOp",EDGE,"E36"),sQuery(id+"F17.wireOp",EDGE,"E41"),sQuery(id+"F18.wireOp",VERTEX,"E45.start"),sQuery(id+"F18.wireOp",VERTEX,"E45.end"),sQuery(id+"F18.wireOp",EDGE,"E45")])]}),makeQuery(id+"F12.boolean.opBoolean","COPY",FACE,{"disambiguationData":[TD([makeQuery(id+"F5.opExtrude","SWEPT_FACE",FACE,{"disambiguationData":[OSD([sQuery(id+"F3.wireOp",EDGE,"E12")])]})])],"derivedFrom":subQ8}),makeQuery(id+"F12.boolean.opBoolean","COPY",FACE,{"disambiguationData":[TD([makeQuery(id+"F1.opExtrude","SWEPT_FACE",FACE,{"disambiguationData":[OSD([subQ6])]})])],"derivedFrom":subQ8})]});}
            extrude(context, id + "F31", {"entities" : qUnion([Q0]), "operationType" : NewBodyOperationType.ADD, "endBound" : BoundingType.UP_TO_SURFACE, "endBoundEntityFace" : qUnion([Q1]), "depth" : 1 * mm});
        }
        {
            var Q0;
            Q0=makeQuery(id+"F1.opExtrude","SWEPT_BODY",BODY,{"disambiguationData":[OSD([sQuery(id+"F0.wireOp",EDGE,"E0"),sQuery(id+"F0.wireOp",EDGE,"E1"),sQuery(id+"F0.wireOp",EDGE,"E2"),sQuery(id+"F0.wireOp",EDGE,"E3"),sQuery(id+"F0.wireOp",EDGE,"E4"),sQuery(id+"F0.wireOp",EDGE,"E5"),sQuery(id+"F0.wireOp",EDGE,"E6.filletArc"),sQuery(id+"F0.wireOp",EDGE,"E7.filletArc")])]});
            var Q1;
            Q1=makeQuery(id+"F23.opBoolean","MERGE",FACE,{"derivedFrom":[makeQuery(id+"F20.opLoft","SWEPT_FACE",FACE,{"disambiguationData":[OSD([sQuery(id+"F0.wireOp",EDGE,"E0"),sQuery(id+"F13.wireOp",EDGE,"E22.bottom"),sQuery(id+"F15.wireOp",EDGE,"E28.1"),sQuery(id+"F15.wireOp",EDGE,"E34.0"),sQuery(id+"F15.wireOp",EDGE,"E35.0"),sQuery(id+"F17.wireOp",EDGE,"E39"),sQuery(id+"F17.wireOp",EDGE,"E40"),sQuery(id+"F19.wireOp",VERTEX,"E46.start"),sQuery(id+"F19.wireOp",VERTEX,"E46.end"),sQuery(id+"F19.wireOp",EDGE,"E46")])]}),makeQuery(id+"F1.opExtrude","SWEPT_FACE",FACE,{"disambiguationData":[OSD([sQuery(id+"F0.wireOp",EDGE,"E5")])]}),makeQuery(id+"F10.opExtrude","CAP_FACE",FACE,{"disambiguationData":[OSD([sQuery(id+"F4.wireOp",EDGE,"E15"),sQuery(id+"F4.wireOp",EDGE,"E16"),sQuery(id+"F4.wireOp",EDGE,"E17")])],"isStart":true})]});
            mirror(context, id + "F32", {"operationType" : NewBodyOperationType.ADD, "entities" : qUnion([Q0]), "mirrorPlane" : qUnion([Q1])});
        }
        {
            var Q0;
            Q0=qCreatedBy(makeId("Top.planeOp"),FACE);
            var sketch = newSketch(context, id + "F33", { "sketchPlane" : qUnion([Q0])});
            skLineSegment(sketch, "E57.bottom", {"start": v(35.58, 28.11) * mm, "end": v(-50.96, 28.11) * mm});
            skLineSegment(sketch, "E57.top", {"start": v(35.58, -50) * mm, "end": v(-50.96, -50) * mm});
            skLineSegment(sketch, "E57.left", {"start": v(35.58, 28.11) * mm, "end": v(35.58, -50) * mm});
            skLineSegment(sketch, "E57.right", {"start": v(-50.96, 28.11) * mm, "end": v(-50.96, -50) * mm});
            skSolve(sketch);
        }
        {
            var Q0;
            Q0 = qSketchRegion(id + "F33", true);
            extrude(context, id + "F34", {"entities" : qUnion([Q0]), "operationType" : NewBodyOperationType.REMOVE, "endBound" : BoundingType.SYMMETRIC, "oppositeDirection" : true, "depth" : 200 * mm, "offsetDistance" : 25 * mm});
        }
    });
